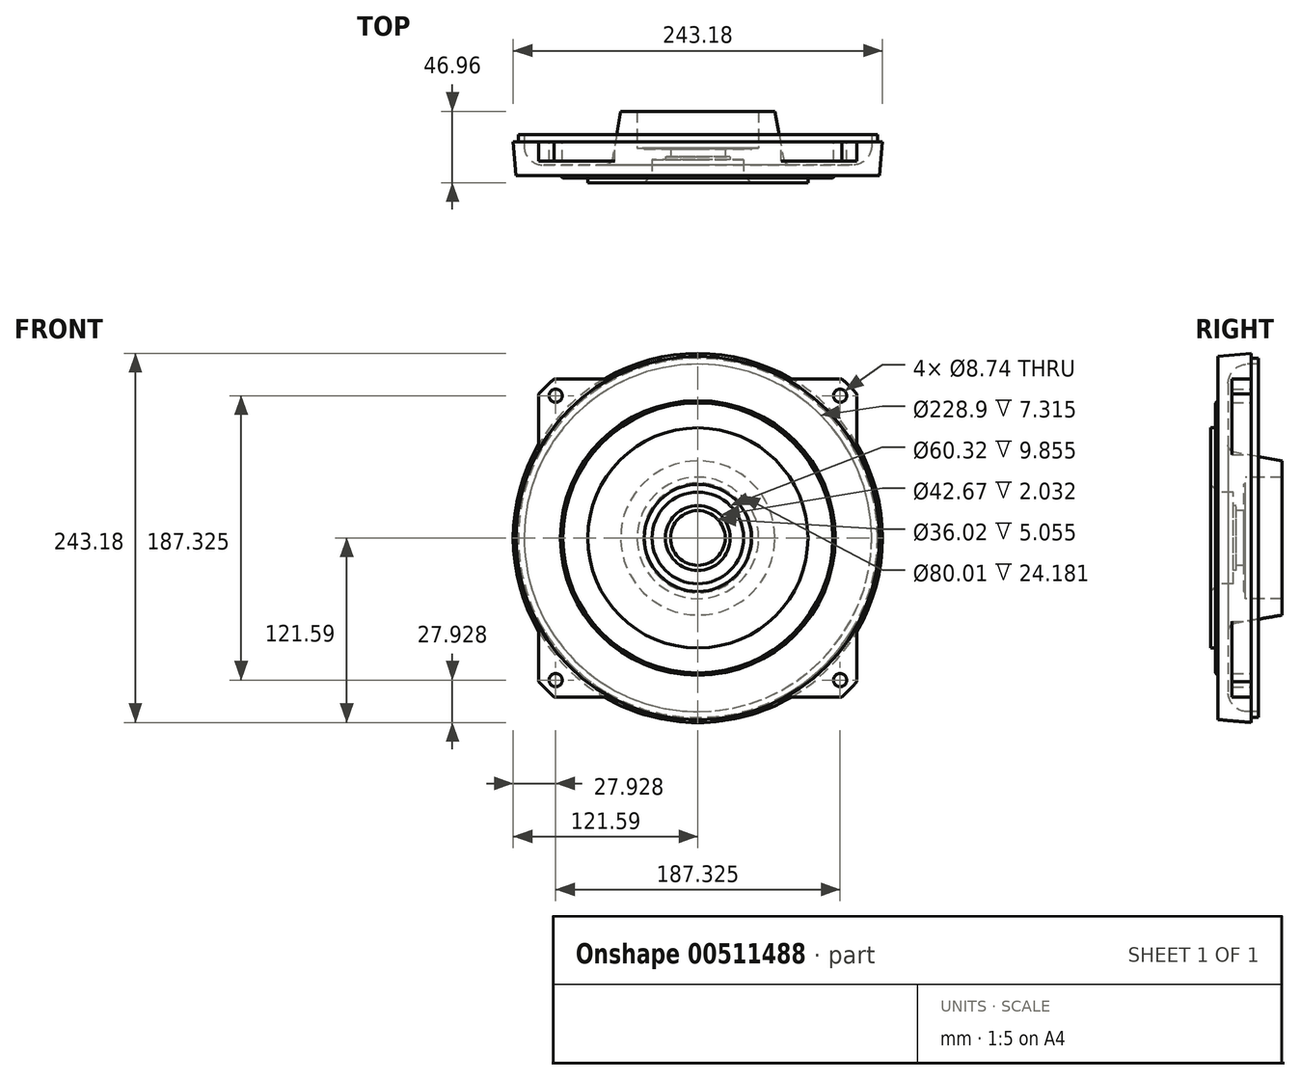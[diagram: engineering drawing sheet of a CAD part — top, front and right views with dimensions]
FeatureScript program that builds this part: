
annotation { "Feature Type Name" : "Feature", "Feature Type Description" : "" }
export const myFeature = defineFeature(function(context is Context, id is Id, definition is map)
    precondition{}
    {
        {
            var Q0;
            Q0=qCreatedBy(makeId("Right.planeOp"),FACE);
            var sketch = newSketch(context, id + "F0", { "sketchPlane" : qUnion([Q0])});
            skLineSegment(sketch, "E0", {"start": v(0, 0) * mm, "end": v(131.03, 0) * mm, "construction": true});
            skLineSegment(sketch, "E1", {"start": v(0, 35.24) * mm, "end": v(0, 72.5) * mm});
            skLineSegment(sketch, "E2", {"start": v(0, 72.5) * mm, "end": v(3.17, 72.5) * mm});
            skLineSegment(sketch, "E3", {"start": v(3.17, 72.5) * mm, "end": v(3.17, 88.9) * mm});
            skLineSegment(sketch, "E4", {"start": v(3.17, 88.9) * mm, "end": v(4.76, 90.49) * mm});
            skLineSegment(sketch, "E5", {"start": v(4.76, 90.49) * mm, "end": v(4.76, 119.66) * mm});
            skLineSegment(sketch, "E6", {"start": v(4.76, 119.66) * mm, "end": v(26.8, 121.59) * mm});
            skLineSegment(sketch, "E7", {"start": v(26.8, 121.59) * mm, "end": v(26.8, 118.26) * mm});
            skLineSegment(sketch, "E8", {"start": v(26.8, 118.26) * mm, "end": v(31.57, 118.26) * mm});
            skLineSegment(sketch, "E9", {"start": v(31.57, 118.26) * mm, "end": v(31.57, 114.45) * mm});
            skLineSegment(sketch, "E10", {"start": v(31.57, 114.45) * mm, "end": v(23.48, 114.45) * mm});
            skLineSegment(sketch, "E11", {"start": v(11.56, 114.45) * mm, "end": v(11.56, 57.04) * mm});
            skLineSegment(sketch, "E12", {"start": v(11.56, 57.04) * mm, "end": v(46.96, 50.8) * mm});
            skLineSegment(sketch, "E13", {"start": v(46.96, 50.8) * mm, "end": v(46.96, 40) * mm});
            skLineSegment(sketch, "E14", {"start": v(46.96, 40) * mm, "end": v(22.78, 40) * mm});
            skLineSegment(sketch, "E15", {"start": v(22.78, 40) * mm, "end": v(22.78, 36.2) * mm});
            skLineSegment(sketch, "E16", {"start": v(22.78, 36.2) * mm, "end": v(22.02, 35.43) * mm});
            skLineSegment(sketch, "E17", {"start": v(22.02, 35.43) * mm, "end": v(22.02, 18) * mm});
            skLineSegment(sketch, "E18", {"start": v(22.02, 18) * mm, "end": v(16.97, 18) * mm});
            skLineSegment(sketch, "E19", {"start": v(16.97, 18) * mm, "end": v(16.97, 21.34) * mm});
            skLineSegment(sketch, "E20", {"start": v(16.97, 21.34) * mm, "end": v(14.94, 21.34) * mm});
            skLineSegment(sketch, "E21", {"start": v(14.94, 21.34) * mm, "end": v(14.94, 30.16) * mm});
            skLineSegment(sketch, "E22", {"start": v(14.94, 30.16) * mm, "end": v(5.08, 30.16) * mm});
            skLineSegment(sketch, "E23", {"start": v(5.08, 30.16) * mm, "end": v(0, 35.24) * mm});
            skLineSegment(sketch, "E24", {"start": v(23.48, 114.45) * mm, "end": v(11.56, 114.45) * mm});
            skSolve(sketch);
        }
        {
            var Q0;
            Q0=makeQuery(id+"F0.imprint","IMPRINT",FACE,{"disambiguationData":[TD([[makeQuery(id+"F0.imprint","IMPRINT",EDGE,{"derivedFrom":sQuery(id+"F0.wireOp",EDGE,"E1")}),-1.0]])]});
            var Q1;
            Q1=sQuery(id+"F0.wireOp",EDGE,"E0");
            revolve(context, id + "F1", {"entities" : qUnion([Q0]), "axis" : qUnion([Q1]), "revolveType" : RevolveType.FULL});
        }
        {
            var Q0;
            Q0=makeQuery(id+"F1.opRevolve","SWEPT_EDGE",EDGE,{"disambiguationData":[OSD([sQuery(id+"F0.wireOp",EDGE,"E11"),sQuery(id+"F0.wireOp",EDGE,"E24")])]});
            fillet(context, id + "F2", {"entities" : qUnion([Q0]), "radius" : 12.7 * mm, "tangentPropagation" : true, "allowEdgeOverflow" : false});
        }
        {
            var Q0;
            Q0=makeQuery(id+"F1.opRevolve","SWEPT_EDGE",EDGE,{"disambiguationData":[OSD([sQuery(id+"F0.wireOp",EDGE,"E11"),sQuery(id+"F0.wireOp",EDGE,"E12")])]});
            fillet(context, id + "F3", {"entities" : qUnion([Q0]), "radius" : 5.08 * mm, "tangentPropagation" : true, "allowEdgeOverflow" : false});
        }
        {
            var Q0;
            Q0=makeQuery(id+"F1.opRevolve","SWEPT_FACE",FACE,{"disambiguationData":[OSD([sQuery(id+"F0.wireOp",EDGE,"E7")])]});
            var sketch = newSketch(context, id + "F4", { "sketchPlane" : qUnion([Q0])});
            skLineSegment(sketch, "E25", {"start": v(139.88, 0) * mm, "end": v(0, 0) * mm, "construction": true});
            skLineSegment(sketch, "E26", {"start": v(0, 0) * mm, "end": v(106.8, 106.8) * mm, "construction": true});
            skArc(sketch, "E27", {"start": v(104.77, 94.79) * mm, "mid": v(99.9, 99.9) * mm, "end": v(94.79, 104.78) * mm});
            skCircle(sketch, "E28", {"center": v(93.66, 93.66) * mm, "radius": 4.37 * mm});
            skLineSegment(sketch, "E29", {"start": v(106.33, 104.78) * mm, "end": v(104.77, 104.78) * mm});
            skLineSegment(sketch, "E30", {"start": v(104.77, 94.79) * mm, "end": v(104.77, 54.84) * mm});
            skLineSegment(sketch, "E31.trimOffspring", {"start": v(94.79, 104.78) * mm, "end": v(54.84, 104.78) * mm});
            skCircle(sketch, "E32", {"center": v(0, 0) * mm, "radius": 118.26 * mm, "construction": true});
            skArc(sketch, "E33", {"start": v(104.77, 54.84) * mm, "mid": v(83.62, 83.62) * mm, "end": v(54.84, 104.77) * mm});
            skSolve(sketch);
        }
        {
            var Q0;
            Q0=makeQuery(id+"F4.imprint","IMPRINT",FACE,{"disambiguationData":[TD([[makeQuery(id+"F4.imprint","IMPRINT",EDGE,{"derivedFrom":sQuery(id+"F4.wireOp",EDGE,"E27")}),1.0]])]});
            var Q1;
            {var subQ0=sQuery(id+"F4.wireOp",EDGE,"E30");var subQ1=sQuery(id+"F0.wireOp",EDGE,"E7");var subQ2=makeQuery(id+"F1.opRevolve","SWEPT_EDGE",EDGE,{"disambiguationData":[OSD([sQuery(id+"F0.wireOp",EDGE,"E6"),subQ1])]});var subQ3=makeQuery(id+"F4.imprint","INTERSECT",VERTEX,{"derivedFrom":[subQ2,subQ0]});Q1=makeQuery(id+"F4.imprint","IMPRINT",FACE,{"disambiguationData":[TD([[makeQuery(id+"F4.imprint","IMPRINT",EDGE,{"disambiguationData":[TD([[subQ3,-1.0]])],"derivedFrom":subQ0}),-1.0]])]});}
            extrude(context, id + "F5", {"entities" : qUnion([Q0, Q1]), "oppositeDirection" : true, "depth" : 12.7 * mm});
        }
        {
            var Q0;
            Q0=makeQuery(id+"F5.opExtrude","SWEPT_BODY",BODY,{"disambiguationData":[OSD([sQuery(id+"F4.wireOp",EDGE,"E27"),sQuery(id+"F4.wireOp",EDGE,"E28"),sQuery(id+"F4.wireOp",EDGE,"E30"),sQuery(id+"F4.wireOp",EDGE,"E31.trimOffspring"),sQuery(id+"F4.wireOp",EDGE,"nL8XCXTk-0rSz-aOC1-my24-eNaaQdnNVz7j")])]});
            var Q1;
            Q1=makeQuery(id+"F1.opRevolve","SWEPT_EDGE",EDGE,{"disambiguationData":[OSD([sQuery(id+"F0.wireOp",EDGE,"E18"),sQuery(id+"F0.wireOp",EDGE,"E19")])]});
            circularPattern(context, id + "F6", {"entities" : qUnion([Q0]), "axis" : qUnion([Q1]), "angle" : 360 * degree, "instanceCount" : 4, "equalSpace" : true});
        }
    });
